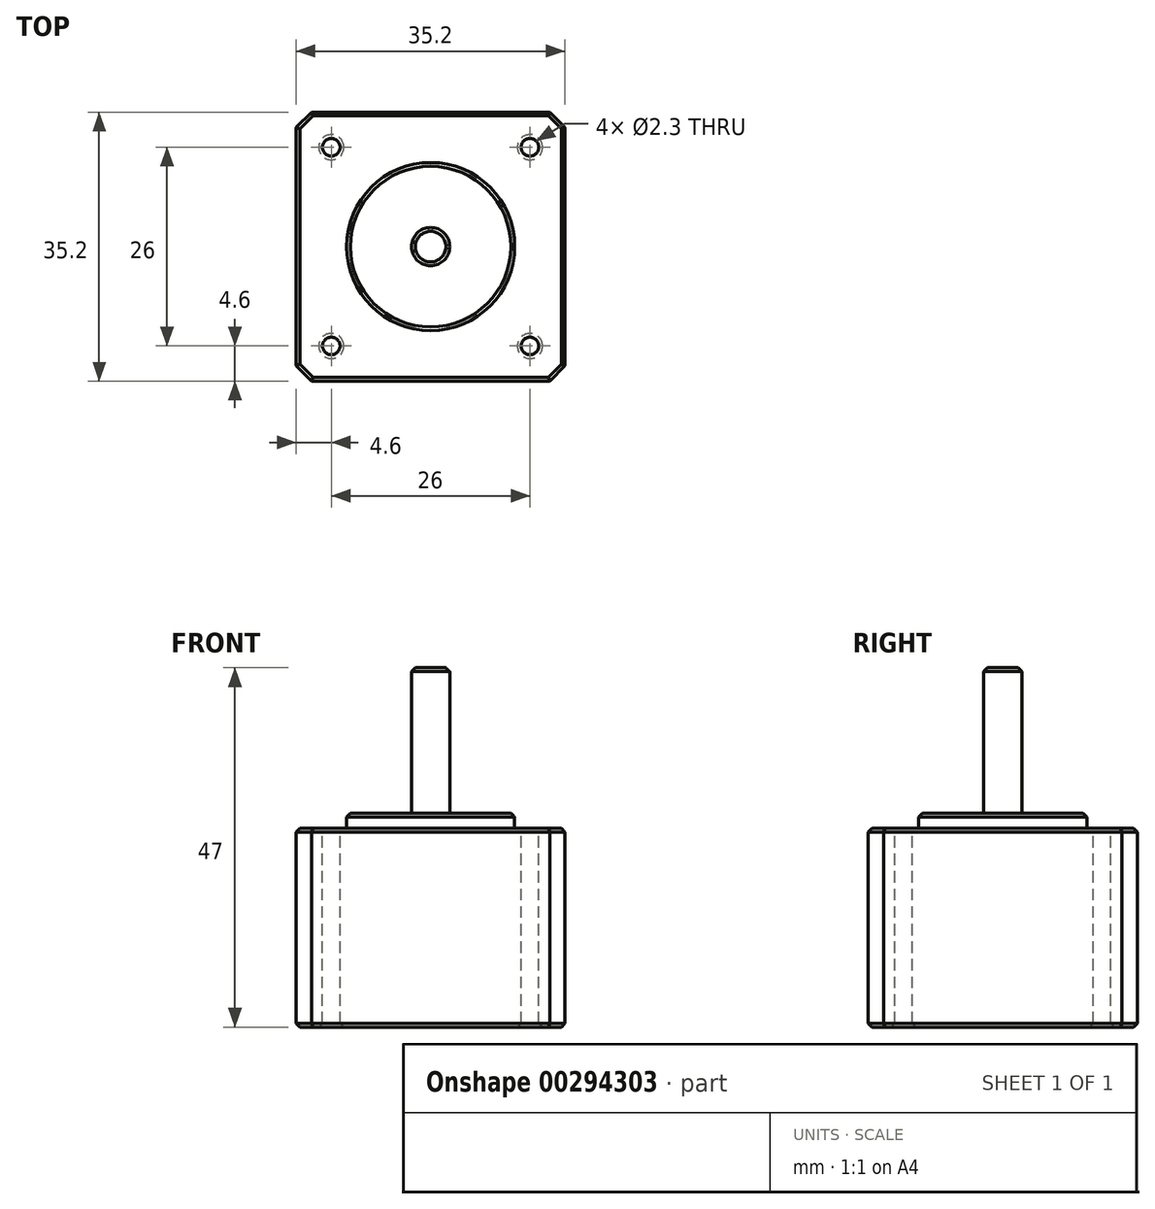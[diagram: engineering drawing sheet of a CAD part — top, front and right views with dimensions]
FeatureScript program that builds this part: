
annotation { "Feature Type Name" : "Feature", "Feature Type Description" : "" }
export const myFeature = defineFeature(function(context is Context, id is Id, definition is map)
    precondition{}
    {
        {
            var Q0;
            Q0=qCreatedBy(makeId("Top.planeOp"),FACE);
            var sketch = newSketch(context, id + "F0", { "sketchPlane" : qUnion([Q0])});
            skLineSegment(sketch, "E0.bottom", {"start": v(-17.6, 17.6) * mm, "end": v(17.6, 17.6) * mm});
            skLineSegment(sketch, "E0.top", {"start": v(-17.6, -17.6) * mm, "end": v(17.6, -17.6) * mm});
            skLineSegment(sketch, "E0.left", {"start": v(-17.6, 17.6) * mm, "end": v(-17.6, -17.6) * mm});
            skLineSegment(sketch, "E0.right", {"start": v(17.6, 17.6) * mm, "end": v(17.6, -17.6) * mm});
            skSolve(sketch);
        }
        {
            var Q0;
            Q0=qCreatedBy(makeId("Top.planeOp"),FACE);
            var sketch = newSketch(context, id + "F1", { "sketchPlane" : qUnion([Q0])});
            skCircle(sketch, "E1", {"center": v(0, 0) * mm, "radius": 11 * mm});
            skSolve(sketch);
        }
        {
            var Q0;
            Q0=qCreatedBy(makeId("Top.planeOp"),FACE);
            var sketch = newSketch(context, id + "F2", { "sketchPlane" : qUnion([Q0])});
            skCircle(sketch, "E2", {"center": v(0, 0) * mm, "radius": 2.5 * mm});
            skSolve(sketch);
        }
        {
            var Q0;
            Q0=qCreatedBy(makeId("Top.planeOp"),FACE);
            var sketch = newSketch(context, id + "F3", { "sketchPlane" : qUnion([Q0])});
            skCircle(sketch, "E3", {"center": v(-13, -13) * mm, "radius": 1.15 * mm});
            skCircle(sketch, "E4", {"center": v(13, -13) * mm, "radius": 1.15 * mm});
            skCircle(sketch, "E5", {"center": v(13, 13) * mm, "radius": 1.15 * mm});
            skCircle(sketch, "E6", {"center": v(-13, 13) * mm, "radius": 1.15 * mm});
            skLineSegment(sketch, "E7.0", {"start": v(-13, 13) * mm, "end": v(13, 13) * mm, "construction": true});
            skLineSegment(sketch, "E7.1", {"start": v(-13, 13) * mm, "end": v(-13, -13) * mm, "construction": true});
            skLineSegment(sketch, "E7.2", {"start": v(-13, -13) * mm, "end": v(13, -13) * mm, "construction": true});
            skLineSegment(sketch, "E7.3", {"start": v(13, 13) * mm, "end": v(13, -13) * mm, "construction": true});
            skSolve(sketch);
        }
        {
            var Q0;
            Q0=makeQuery(id+"F0.imprint","IMPRINT",FACE,{"disambiguationData":[TD([[makeQuery(id+"F0.imprint","IMPRINT",EDGE,{"derivedFrom":sQuery(id+"F0.wireOp",EDGE,"E0.bottom")}),-1.0]])]});
            extrude(context, id + "F4", {"entities" : qUnion([Q0]), "oppositeDirection" : true, "depth" : 26 * mm});
        }
        {
            var Q0;
            Q0 = qSketchRegion(id + "F1", true);
            extrude(context, id + "F5", {"entities" : qUnion([Q0]), "operationType" : NewBodyOperationType.ADD, "depth" : 2 * mm});
        }
        {
            var Q0;
            Q0 = qSketchRegion(id + "F2", true);
            var Q1;
            Q1=sQuery(id+"F2.wireOp",EDGE,"E2");
            extrude(context, id + "F6", {"entities" : qUnion([Q0]), "operationType" : NewBodyOperationType.ADD, "surfaceEntities" : qUnion([Q1]), "depth" : 21 * mm});
        }
        {
            var Q0;
            Q0 = qSketchRegion(id + "F3", true);
            var Q1;
            Q1=sQuery(id+"F3.wireOp",EDGE,"E5");
            var Q2;
            Q2=sQuery(id+"F3.wireOp",EDGE,"E6");
            var Q3;
            Q3=sQuery(id+"F3.wireOp",EDGE,"E3");
            var Q4;
            Q4=sQuery(id+"F3.wireOp",EDGE,"E4");
            extrude(context, id + "F7", {"entities" : qUnion([Q0]), "operationType" : NewBodyOperationType.REMOVE, "surfaceEntities" : qUnion([Q1, Q2, Q3, Q4]), "endBound" : BoundingType.THROUGH_ALL, "oppositeDirection" : true, "depth" : 25 * mm});
        }
        {
            var Q0;
            Q0=makeQuery(id+"F4.opExtrude","SWEPT_EDGE",EDGE,{"disambiguationData":[OSD([sQuery(id+"F0.wireOp",EDGE,"E0.top"),sQuery(id+"F0.wireOp",EDGE,"E0.right")])]});
            var Q1;
            Q1=makeQuery(id+"F4.opExtrude","SWEPT_EDGE",EDGE,{"disambiguationData":[OSD([sQuery(id+"F0.wireOp",EDGE,"E0.top"),sQuery(id+"F0.wireOp",EDGE,"E0.left")])]});
            var Q2;
            Q2=makeQuery(id+"F4.opExtrude","SWEPT_EDGE",EDGE,{"disambiguationData":[OSD([sQuery(id+"F0.wireOp",EDGE,"E0.bottom"),sQuery(id+"F0.wireOp",EDGE,"E0.left")])]});
            var Q3;
            Q3=makeQuery(id+"F4.opExtrude","SWEPT_EDGE",EDGE,{"disambiguationData":[OSD([sQuery(id+"F0.wireOp",EDGE,"E0.bottom"),sQuery(id+"F0.wireOp",EDGE,"E0.right")])]});
            chamfer(context, id + "F8", {"entities" : qUnion([Q0, Q1, Q2, Q3]), "width" : 2 * mm, "tangentPropagation" : true});
        }
        {
            var Q0;
            Q0=makeQuery(id+"F6.opExtrude","CAP_EDGE",EDGE,{"disambiguationData":[OSD([sQuery(id+"F2.wireOp",EDGE,"E2")])],"isStart":false});
            var Q1;
            Q1=makeQuery(id+"F5.opExtrude","CAP_EDGE",EDGE,{"disambiguationData":[OSD([sQuery(id+"F1.wireOp",EDGE,"E1")])],"isStart":false});
            var Q2;
            Q2=makeQuery(id+"F7.boolean.opBoolean","COPY",EDGE,{"derivedFrom":makeQuery(id+"F7.opExtrude","CAP_EDGE",EDGE,{"disambiguationData":[OSD([sQuery(id+"F3.wireOp",EDGE,"E5")])],"isStart":true})});
            var Q3;
            Q3=makeQuery(id+"F7.boolean.opBoolean","COPY",EDGE,{"derivedFrom":makeQuery(id+"F7.opExtrude","CAP_EDGE",EDGE,{"disambiguationData":[OSD([sQuery(id+"F3.wireOp",EDGE,"E4")])],"isStart":true})});
            var Q4;
            Q4=makeQuery(id+"F7.boolean.opBoolean","COPY",EDGE,{"derivedFrom":makeQuery(id+"F7.opExtrude","CAP_EDGE",EDGE,{"disambiguationData":[OSD([sQuery(id+"F3.wireOp",EDGE,"E3")])],"isStart":true})});
            var Q5;
            Q5=makeQuery(id+"F7.boolean.opBoolean","COPY",EDGE,{"derivedFrom":makeQuery(id+"F7.opExtrude","CAP_EDGE",EDGE,{"disambiguationData":[OSD([sQuery(id+"F3.wireOp",EDGE,"E6")])],"isStart":true})});
            var Q6;
            Q6=makeQuery(id+"F4.opExtrude","CAP_EDGE",EDGE,{"disambiguationData":[OSD([sQuery(id+"F0.wireOp",EDGE,"E0.bottom")])],"isStart":true});
            var Q7;
            {var subQ0=sQuery(id+"F0.wireOp",EDGE,"E0.right");var subQ1=sQuery(id+"F0.wireOp",EDGE,"E0.bottom");Q7=makeQuery(id+"F8.opChamfer","BLEND_EDGE",EDGE,{"blendedFrom":[makeQuery(id+"F4.opExtrude","SWEPT_EDGE",EDGE,{"disambiguationData":[OSD([subQ1,subQ0])]}),makeQuery(id+"F4.opExtrude","CAP_FACE",FACE,{"disambiguationData":[OSD([subQ1,sQuery(id+"F0.wireOp",EDGE,"E0.top"),sQuery(id+"F0.wireOp",EDGE,"E0.left"),subQ0])],"isStart":true})],"blendedInto":[makeQuery(id+"F4.opExtrude","CAP_FACE",FACE,{"disambiguationData":[OSD([subQ1,sQuery(id+"F0.wireOp",EDGE,"E0.top"),sQuery(id+"F0.wireOp",EDGE,"E0.left"),subQ0])],"isStart":true})]});}
            var Q8;
            Q8=makeQuery(id+"F4.opExtrude","CAP_EDGE",EDGE,{"disambiguationData":[OSD([sQuery(id+"F0.wireOp",EDGE,"E0.right")])],"isStart":true});
            var Q9;
            {var subQ0=sQuery(id+"F0.wireOp",EDGE,"E0.right");var subQ1=sQuery(id+"F0.wireOp",EDGE,"E0.top");Q9=makeQuery(id+"F8.opChamfer","BLEND_EDGE",EDGE,{"blendedFrom":[makeQuery(id+"F4.opExtrude","SWEPT_EDGE",EDGE,{"disambiguationData":[OSD([subQ1,subQ0])]}),makeQuery(id+"F4.opExtrude","CAP_FACE",FACE,{"disambiguationData":[OSD([sQuery(id+"F0.wireOp",EDGE,"E0.bottom"),subQ1,sQuery(id+"F0.wireOp",EDGE,"E0.left"),subQ0])],"isStart":true})],"blendedInto":[makeQuery(id+"F4.opExtrude","CAP_FACE",FACE,{"disambiguationData":[OSD([sQuery(id+"F0.wireOp",EDGE,"E0.bottom"),subQ1,sQuery(id+"F0.wireOp",EDGE,"E0.left"),subQ0])],"isStart":true})]});}
            var Q10;
            Q10=makeQuery(id+"F4.opExtrude","CAP_EDGE",EDGE,{"disambiguationData":[OSD([sQuery(id+"F0.wireOp",EDGE,"E0.top")])],"isStart":true});
            var Q11;
            Q11=makeQuery(id+"F4.opExtrude","CAP_EDGE",EDGE,{"disambiguationData":[OSD([sQuery(id+"F0.wireOp",EDGE,"E0.left")])],"isStart":true});
            var Q12;
            Q12=makeQuery(id+"F4.opExtrude","CAP_EDGE",EDGE,{"disambiguationData":[OSD([sQuery(id+"F0.wireOp",EDGE,"E0.right")])],"isStart":false});
            var Q13;
            Q13=makeQuery(id+"F4.opExtrude","CAP_EDGE",EDGE,{"disambiguationData":[OSD([sQuery(id+"F0.wireOp",EDGE,"E0.top")])],"isStart":false});
            var Q14;
            Q14=makeQuery(id+"F7.boolean.opBoolean","INTERSECT",EDGE,{"derivedFrom":[makeQuery(id+"F4.opExtrude","CAP_FACE",FACE,{"disambiguationData":[OSD([sQuery(id+"F0.wireOp",EDGE,"E0.bottom"),sQuery(id+"F0.wireOp",EDGE,"E0.top"),sQuery(id+"F0.wireOp",EDGE,"E0.left"),sQuery(id+"F0.wireOp",EDGE,"E0.right")])],"isStart":false}),makeQuery(id+"F7.opExtrude","SWEPT_FACE",FACE,{"disambiguationData":[OSD([sQuery(id+"F3.wireOp",EDGE,"E4")])]})]});
            var Q15;
            {var subQ0=sQuery(id+"F0.wireOp",EDGE,"E0.right");var subQ1=sQuery(id+"F0.wireOp",EDGE,"E0.top");Q15=makeQuery(id+"F8.opChamfer","BLEND_EDGE",EDGE,{"blendedFrom":[makeQuery(id+"F4.opExtrude","SWEPT_EDGE",EDGE,{"disambiguationData":[OSD([subQ1,subQ0])]}),makeQuery(id+"F4.opExtrude","CAP_FACE",FACE,{"disambiguationData":[OSD([sQuery(id+"F0.wireOp",EDGE,"E0.bottom"),subQ1,sQuery(id+"F0.wireOp",EDGE,"E0.left"),subQ0])],"isStart":false})],"blendedInto":[makeQuery(id+"F4.opExtrude","CAP_FACE",FACE,{"disambiguationData":[OSD([sQuery(id+"F0.wireOp",EDGE,"E0.bottom"),subQ1,sQuery(id+"F0.wireOp",EDGE,"E0.left"),subQ0])],"isStart":false})]});}
            var Q16;
            Q16=makeQuery(id+"F7.boolean.opBoolean","INTERSECT",EDGE,{"derivedFrom":[makeQuery(id+"F4.opExtrude","CAP_FACE",FACE,{"disambiguationData":[OSD([sQuery(id+"F0.wireOp",EDGE,"E0.bottom"),sQuery(id+"F0.wireOp",EDGE,"E0.top"),sQuery(id+"F0.wireOp",EDGE,"E0.left"),sQuery(id+"F0.wireOp",EDGE,"E0.right")])],"isStart":false}),makeQuery(id+"F7.opExtrude","SWEPT_FACE",FACE,{"disambiguationData":[OSD([sQuery(id+"F3.wireOp",EDGE,"E3")])]})]});
            var Q17;
            Q17=makeQuery(id+"F7.boolean.opBoolean","INTERSECT",EDGE,{"derivedFrom":[makeQuery(id+"F4.opExtrude","CAP_FACE",FACE,{"disambiguationData":[OSD([sQuery(id+"F0.wireOp",EDGE,"E0.bottom"),sQuery(id+"F0.wireOp",EDGE,"E0.top"),sQuery(id+"F0.wireOp",EDGE,"E0.left"),sQuery(id+"F0.wireOp",EDGE,"E0.right")])],"isStart":false}),makeQuery(id+"F7.opExtrude","SWEPT_FACE",FACE,{"disambiguationData":[OSD([sQuery(id+"F3.wireOp",EDGE,"E5")])]})]});
            var Q18;
            Q18=makeQuery(id+"F7.boolean.opBoolean","INTERSECT",EDGE,{"derivedFrom":[makeQuery(id+"F4.opExtrude","CAP_FACE",FACE,{"disambiguationData":[OSD([sQuery(id+"F0.wireOp",EDGE,"E0.bottom"),sQuery(id+"F0.wireOp",EDGE,"E0.top"),sQuery(id+"F0.wireOp",EDGE,"E0.left"),sQuery(id+"F0.wireOp",EDGE,"E0.right")])],"isStart":false}),makeQuery(id+"F7.opExtrude","SWEPT_FACE",FACE,{"disambiguationData":[OSD([sQuery(id+"F3.wireOp",EDGE,"E6")])]})]});
            var Q19;
            Q19=makeQuery(id+"F4.opExtrude","CAP_EDGE",EDGE,{"disambiguationData":[OSD([sQuery(id+"F0.wireOp",EDGE,"E0.bottom")])],"isStart":false});
            var Q20;
            {var subQ0=sQuery(id+"F0.wireOp",EDGE,"E0.left");var subQ1=sQuery(id+"F0.wireOp",EDGE,"E0.bottom");Q20=makeQuery(id+"F8.opChamfer","BLEND_EDGE",EDGE,{"blendedFrom":[makeQuery(id+"F4.opExtrude","SWEPT_EDGE",EDGE,{"disambiguationData":[OSD([subQ1,subQ0])]}),makeQuery(id+"F4.opExtrude","CAP_FACE",FACE,{"disambiguationData":[OSD([subQ1,sQuery(id+"F0.wireOp",EDGE,"E0.top"),subQ0,sQuery(id+"F0.wireOp",EDGE,"E0.right")])],"isStart":false})],"blendedInto":[makeQuery(id+"F4.opExtrude","CAP_FACE",FACE,{"disambiguationData":[OSD([subQ1,sQuery(id+"F0.wireOp",EDGE,"E0.top"),subQ0,sQuery(id+"F0.wireOp",EDGE,"E0.right")])],"isStart":false})]});}
            var Q21;
            {var subQ0=sQuery(id+"F0.wireOp",EDGE,"E0.right");var subQ1=sQuery(id+"F0.wireOp",EDGE,"E0.bottom");Q21=makeQuery(id+"F8.opChamfer","BLEND_EDGE",EDGE,{"blendedFrom":[makeQuery(id+"F4.opExtrude","SWEPT_EDGE",EDGE,{"disambiguationData":[OSD([subQ1,subQ0])]}),makeQuery(id+"F4.opExtrude","CAP_FACE",FACE,{"disambiguationData":[OSD([subQ1,sQuery(id+"F0.wireOp",EDGE,"E0.top"),sQuery(id+"F0.wireOp",EDGE,"E0.left"),subQ0])],"isStart":false})],"blendedInto":[makeQuery(id+"F4.opExtrude","CAP_FACE",FACE,{"disambiguationData":[OSD([subQ1,sQuery(id+"F0.wireOp",EDGE,"E0.top"),sQuery(id+"F0.wireOp",EDGE,"E0.left"),subQ0])],"isStart":false})]});}
            var Q22;
            Q22=makeQuery(id+"F4.opExtrude","CAP_EDGE",EDGE,{"disambiguationData":[OSD([sQuery(id+"F0.wireOp",EDGE,"E0.left")])],"isStart":false});
            var Q23;
            {var subQ0=sQuery(id+"F0.wireOp",EDGE,"E0.left");var subQ1=sQuery(id+"F0.wireOp",EDGE,"E0.top");Q23=makeQuery(id+"F8.opChamfer","BLEND_EDGE",EDGE,{"blendedFrom":[makeQuery(id+"F4.opExtrude","SWEPT_EDGE",EDGE,{"disambiguationData":[OSD([subQ1,subQ0])]}),makeQuery(id+"F4.opExtrude","CAP_FACE",FACE,{"disambiguationData":[OSD([sQuery(id+"F0.wireOp",EDGE,"E0.bottom"),subQ1,subQ0,sQuery(id+"F0.wireOp",EDGE,"E0.right")])],"isStart":false})],"blendedInto":[makeQuery(id+"F4.opExtrude","CAP_FACE",FACE,{"disambiguationData":[OSD([sQuery(id+"F0.wireOp",EDGE,"E0.bottom"),subQ1,subQ0,sQuery(id+"F0.wireOp",EDGE,"E0.right")])],"isStart":false})]});}
            var Q24;
            {var subQ0=sQuery(id+"F0.wireOp",EDGE,"E0.left");var subQ1=sQuery(id+"F0.wireOp",EDGE,"E0.bottom");Q24=makeQuery(id+"F8.opChamfer","BLEND_EDGE",EDGE,{"blendedFrom":[makeQuery(id+"F4.opExtrude","SWEPT_EDGE",EDGE,{"disambiguationData":[OSD([subQ1,subQ0])]}),makeQuery(id+"F4.opExtrude","CAP_FACE",FACE,{"disambiguationData":[OSD([subQ1,sQuery(id+"F0.wireOp",EDGE,"E0.top"),subQ0,sQuery(id+"F0.wireOp",EDGE,"E0.right")])],"isStart":true})],"blendedInto":[makeQuery(id+"F4.opExtrude","CAP_FACE",FACE,{"disambiguationData":[OSD([subQ1,sQuery(id+"F0.wireOp",EDGE,"E0.top"),subQ0,sQuery(id+"F0.wireOp",EDGE,"E0.right")])],"isStart":true})]});}
            var Q25;
            {var subQ0=sQuery(id+"F0.wireOp",EDGE,"E0.left");var subQ1=sQuery(id+"F0.wireOp",EDGE,"E0.top");Q25=makeQuery(id+"F8.opChamfer","BLEND_EDGE",EDGE,{"blendedFrom":[makeQuery(id+"F4.opExtrude","SWEPT_EDGE",EDGE,{"disambiguationData":[OSD([subQ1,subQ0])]}),makeQuery(id+"F4.opExtrude","CAP_FACE",FACE,{"disambiguationData":[OSD([sQuery(id+"F0.wireOp",EDGE,"E0.bottom"),subQ1,subQ0,sQuery(id+"F0.wireOp",EDGE,"E0.right")])],"isStart":true})],"blendedInto":[makeQuery(id+"F4.opExtrude","CAP_FACE",FACE,{"disambiguationData":[OSD([sQuery(id+"F0.wireOp",EDGE,"E0.bottom"),subQ1,subQ0,sQuery(id+"F0.wireOp",EDGE,"E0.right")])],"isStart":true})]});}
            chamfer(context, id + "F9", {"entities" : qUnion([Q0, Q1, Q2, Q3, Q4, Q5, Q6, Q7, Q8, Q9, Q10, Q11, Q12, Q13, Q14, Q15, Q16, Q17, Q18, Q19, Q20, Q21, Q22, Q23, Q24, Q25]), "width" : 0.5 * mm, "tangentPropagation" : true});
        }
    });
